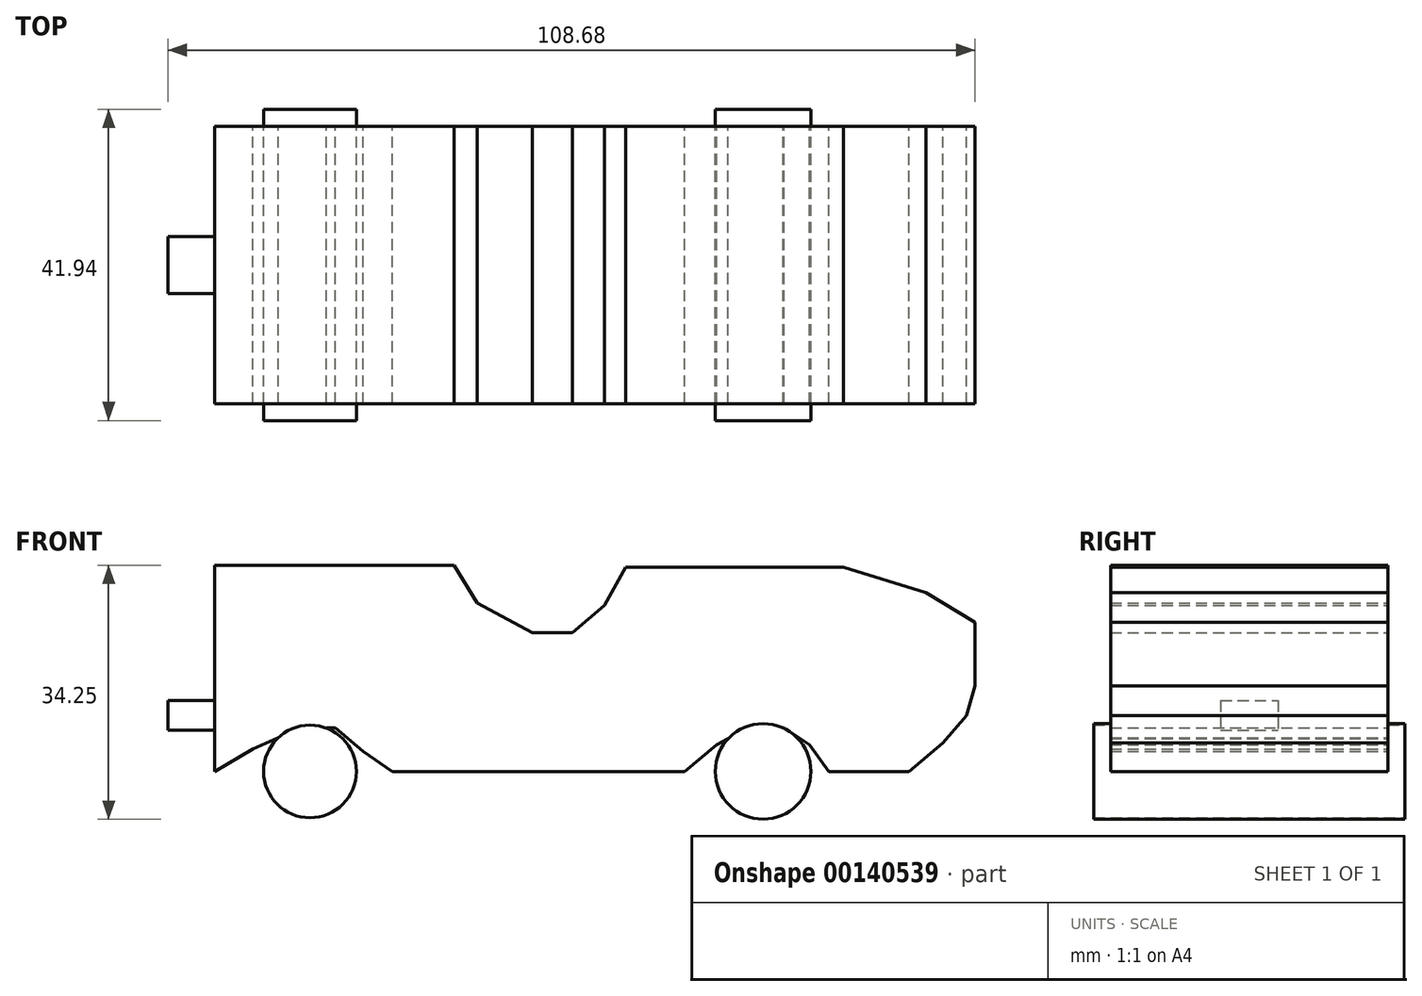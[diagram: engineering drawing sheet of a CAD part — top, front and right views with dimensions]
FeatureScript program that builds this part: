
annotation { "Feature Type Name" : "Feature", "Feature Type Description" : "" }
export const myFeature = defineFeature(function(context is Context, id is Id, definition is map)
    precondition{}
    {
        {
            var Q0;
            Q0=qCreatedBy(makeId("Front.planeOp"),FACE);
            var sketch = newSketch(context, id + "F0", { "sketchPlane" : qUnion([Q0])});
            skLineSegment(sketch, "E0", {"start": v(41.93, 27.53) * mm, "end": v(12.55, 27.53) * mm});
            skLineSegment(sketch, "E1", {"start": v(12.55, 27.53) * mm, "end": v(9.7, 22.4) * mm});
            skLineSegment(sketch, "E2", {"start": v(9.7, 22.4) * mm, "end": v(5.42, 18.68) * mm});
            skLineSegment(sketch, "E3", {"start": v(5.42, 18.68) * mm, "end": v(0, 18.68) * mm});
            skLineSegment(sketch, "E4", {"start": v(0, 18.68) * mm, "end": v(-7.42, 22.68) * mm});
            skLineSegment(sketch, "E5", {"start": v(-7.42, 22.68) * mm, "end": v(-10.55, 27.81) * mm});
            skLineSegment(sketch, "E6", {"start": v(-10.55, 27.81) * mm, "end": v(-42.79, 27.81) * mm});
            skLineSegment(sketch, "E7", {"start": v(-42.79, 27.81) * mm, "end": v(-42.79, 0) * mm});
            skLineSegment(sketch, "E8", {"start": v(-42.79, 0) * mm, "end": v(-37.65, 3) * mm});
            skLineSegment(sketch, "E9", {"start": v(-37.65, 3) * mm, "end": v(-31.38, 5.85) * mm});
            skLineSegment(sketch, "E10", {"start": v(-31.38, 5.85) * mm, "end": v(-26.53, 5.85) * mm});
            skLineSegment(sketch, "E11", {"start": v(-26.53, 5.85) * mm, "end": v(-22.82, 2.7) * mm});
            skLineSegment(sketch, "E12", {"start": v(-22.82, 2.7) * mm, "end": v(-18.83, 0) * mm});
            skLineSegment(sketch, "E13", {"start": v(-18.83, 0) * mm, "end": v(0, 0) * mm});
            skLineSegment(sketch, "E14", {"start": v(0, 0) * mm, "end": v(20.54, 0) * mm});
            skLineSegment(sketch, "E15", {"start": v(20.54, 0) * mm, "end": v(24.82, 3.57) * mm});
            skLineSegment(sketch, "E16", {"start": v(24.82, 3.57) * mm, "end": v(29.1, 5.85) * mm});
            skLineSegment(sketch, "E17", {"start": v(29.1, 5.85) * mm, "end": v(33.94, 5.85) * mm});
            skLineSegment(sketch, "E18", {"start": v(33.94, 5.85) * mm, "end": v(37.37, 3.57) * mm});
            skLineSegment(sketch, "E19", {"start": v(37.37, 3.57) * mm, "end": v(39.93, 0) * mm});
            skLineSegment(sketch, "E20", {"start": v(39.93, 0) * mm, "end": v(45.64, 0) * mm});
            skLineSegment(sketch, "E21", {"start": v(45.64, 0) * mm, "end": v(50.77, 0) * mm});
            skLineSegment(sketch, "E22", {"start": v(50.77, 0) * mm, "end": v(55.34, 3.85) * mm});
            skLineSegment(sketch, "E23", {"start": v(55.34, 3.85) * mm, "end": v(58.47, 7.56) * mm});
            skLineSegment(sketch, "E24", {"start": v(41.93, 27.53) * mm, "end": v(53.05, 24.1) * mm});
            skLineSegment(sketch, "E25", {"start": v(53.05, 24.1) * mm, "end": v(59.62, 20.1) * mm});
            skLineSegment(sketch, "E26", {"start": v(59.62, 20.1) * mm, "end": v(59.62, 11.55) * mm});
            skLineSegment(sketch, "E27", {"start": v(59.62, 11.55) * mm, "end": v(58.47, 7.56) * mm});
            skSolve(sketch);
        }
        {
            var Q0;
            Q0=makeQuery(id+"F0.imprint","IMPRINT",FACE,{"disambiguationData":[TD([[makeQuery(id+"F0.imprint","IMPRINT",EDGE,{"derivedFrom":sQuery(id+"F0.wireOp",EDGE,"E0")}),1.0]])]});
            extrude(context, id + "F1", {"entities" : qUnion([Q0]), "endBound" : BoundingType.SYMMETRIC, "depth" : 37.38 * mm});
        }
        {
            var Q0;
            Q0=qCreatedBy(makeId("Front.planeOp"),FACE);
            var sketch = newSketch(context, id + "F2", { "sketchPlane" : qUnion([Q0])});
            skCircle(sketch, "E28", {"center": v(-29.95, 0) * mm, "radius": 6.25 * mm});
            skSolve(sketch);
        }
        {
            var Q0;
            Q0=makeQuery(id+"F2.imprint","IMPRINT",FACE,{"disambiguationData":[TD([[makeQuery(id+"F2.imprint","IMPRINT",EDGE,{"derivedFrom":sQuery(id+"F2.wireOp",EDGE,"E28")}),1.0]])]});
            extrude(context, id + "F3", {"entities" : qUnion([Q0]), "operationType" : NewBodyOperationType.ADD, "endBound" : BoundingType.SYMMETRIC, "depth" : 41.94 * mm});
        }
        {
            var Q0;
            Q0=qCreatedBy(makeId("Front.planeOp"),FACE);
            var sketch = newSketch(context, id + "F4", { "sketchPlane" : qUnion([Q0])});
            skCircle(sketch, "E29", {"center": v(31.1, 0) * mm, "radius": 6.44 * mm});
            skSolve(sketch);
        }
        {
            var Q0;
            Q0=makeQuery(id+"F4.imprint","IMPRINT",FACE,{"disambiguationData":[TD([[makeQuery(id+"F4.imprint","IMPRINT",EDGE,{"derivedFrom":sQuery(id+"F4.wireOp",EDGE,"E29")}),1.0]])]});
            extrude(context, id + "F5", {"entities" : qUnion([Q0]), "operationType" : NewBodyOperationType.ADD, "endBound" : BoundingType.SYMMETRIC, "depth" : 41.94 * mm});
        }
        {
            var Q0;
            Q0=qCreatedBy(makeId("Front.planeOp"),FACE);
            var sketch = newSketch(context, id + "F6", { "sketchPlane" : qUnion([Q0])});
            skLineSegment(sketch, "E30.bottom", {"start": v(-42.79, 9.56) * mm, "end": v(-49.06, 9.56) * mm});
            skLineSegment(sketch, "E30.top", {"start": v(-42.79, 5.56) * mm, "end": v(-49.06, 5.56) * mm});
            skLineSegment(sketch, "E30.left", {"start": v(-42.79, 9.56) * mm, "end": v(-42.79, 5.56) * mm});
            skLineSegment(sketch, "E30.right", {"start": v(-49.06, 9.56) * mm, "end": v(-49.06, 5.56) * mm});
            skSolve(sketch);
        }
        {
            var Q0;
            Q0=makeQuery(id+"F6.imprint","IMPRINT",FACE,{"disambiguationData":[TD([[makeQuery(id+"F6.imprint","IMPRINT",EDGE,{"derivedFrom":sQuery(id+"F6.wireOp",EDGE,"E30.bottom")}),1.0]])]});
            extrude(context, id + "F7", {"entities" : qUnion([Q0]), "operationType" : NewBodyOperationType.ADD, "endBound" : BoundingType.SYMMETRIC, "depth" : 7.72 * mm});
        }
    });
